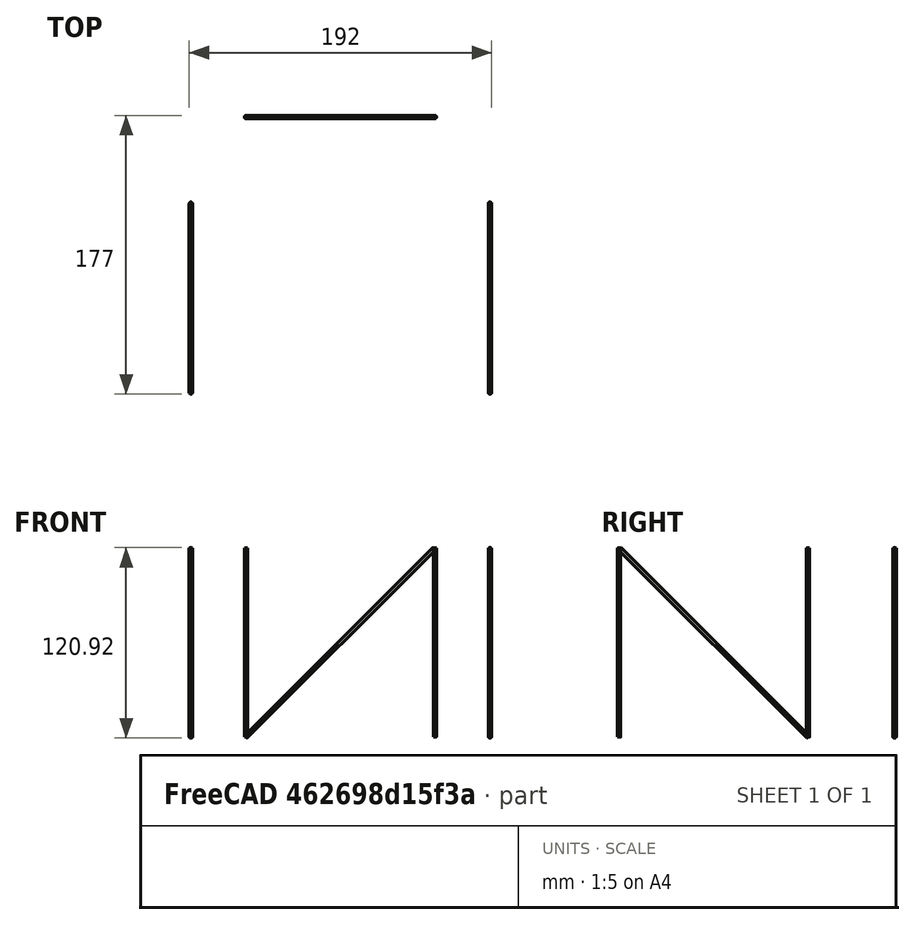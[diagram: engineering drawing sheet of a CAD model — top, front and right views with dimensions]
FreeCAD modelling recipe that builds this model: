
FCSTD DOCUMENT  (FreeCAD 0.19R)
Label: leksell
License: All rights reserved
LicenseURL: http://en.wikipedia.org/wiki/All_rights_reserved
objects: Part::FeaturePython×9, Part::MultiFuse×3
note: 12 computed .brp shape members not serialized (recipe doc carries the construction recipe); baked Part::Feature solids carry a one-line shape summary decoded from their .brp

FEATURE [Part::FeaturePython] Tube001  # WARN: FeaturePython — macro-defined, semantics opaque (R4)
  AttacherType = Attacher::AttachEngine3D
  Height = 120
  InnerRadius = 0
  OuterRadius = 1
  Placement = pos=(-5,40,0) rot=(0,0,1;0rad)
FEATURE [Part::FeaturePython] Tube002  # WARN: FeaturePython — macro-defined, semantics opaque (R4)
  AttacherType = Attacher::AttachEngine3D
  Height = 169
  InnerRadius = 0
  OuterRadius = 1
  Placement = pos=(-5,160,0) rot=(1,0,0;0.785398rad)
FEATURE [Part::FeaturePython] Tube003  # WARN: FeaturePython — macro-defined, semantics opaque (R4)
  AttacherType = Attacher::AttachEngine3D
  Height = 120
  InnerRadius = 0
  OuterRadius = 1
  Placement = pos=(-5,160,0) rot=(0,0,1;0rad)
FEATURE [Part::FeaturePython] Tube004  # WARN: FeaturePython — macro-defined, semantics opaque (R4)
  AttacherType = Attacher::AttachEngine3D
  Height = 120
  InnerRadius = 0
  OuterRadius = 1
  Placement = pos=(-40,215,0) rot=(0,0,1;0rad)
FEATURE [Part::FeaturePython] Tube005  # WARN: FeaturePython — macro-defined, semantics opaque (R4)
  AttacherType = Attacher::AttachEngine3D
  Height = 169
  InnerRadius = 0
  OuterRadius = 1
  Placement = pos=(-160,215,0) rot=(0,1,0;0.785398rad)
FEATURE [Part::FeaturePython] Tube006  # WARN: FeaturePython — macro-defined, semantics opaque (R4)
  AttacherType = Attacher::AttachEngine3D
  Height = 120
  InnerRadius = 0
  OuterRadius = 1
  Placement = pos=(-160,215,0) rot=(0,0,1;0rad)
FEATURE [Part::FeaturePython] Tube007  # WARN: FeaturePython — macro-defined, semantics opaque (R4)
  AttacherType = Attacher::AttachEngine3D
  Height = 120
  InnerRadius = 0
  OuterRadius = 1
  Placement = pos=(-195,40,0) rot=(0,0,1;0rad)
FEATURE [Part::FeaturePython] Tube008  # WARN: FeaturePython — macro-defined, semantics opaque (R4)
  AttacherType = Attacher::AttachEngine3D
  Height = 169
  InnerRadius = 0
  OuterRadius = 1
  Placement = pos=(-195,160,0) rot=(1,0,0;0.785398rad)
FEATURE [Part::FeaturePython] Tube009  # WARN: FeaturePython — macro-defined, semantics opaque (R4)
  AttacherType = Attacher::AttachEngine3D
  Height = 120
  InnerRadius = 0
  OuterRadius = 1
  Placement = pos=(-195,160,0) rot=(0,0,1;0rad)
FEATURE [Part::MultiFuse] Fusion  label="NBar_001"
  Shapes = -> [Tube003,Tube001,Tube002]
FEATURE [Part::MultiFuse] Fusion001  label="NBar_002"
  Shapes = -> [Tube004,Tube005,Tube006]
FEATURE [Part::MultiFuse] Fusion002  label="NBar_003"
  Shapes = -> [Tube007,Tube008,Tube009]
